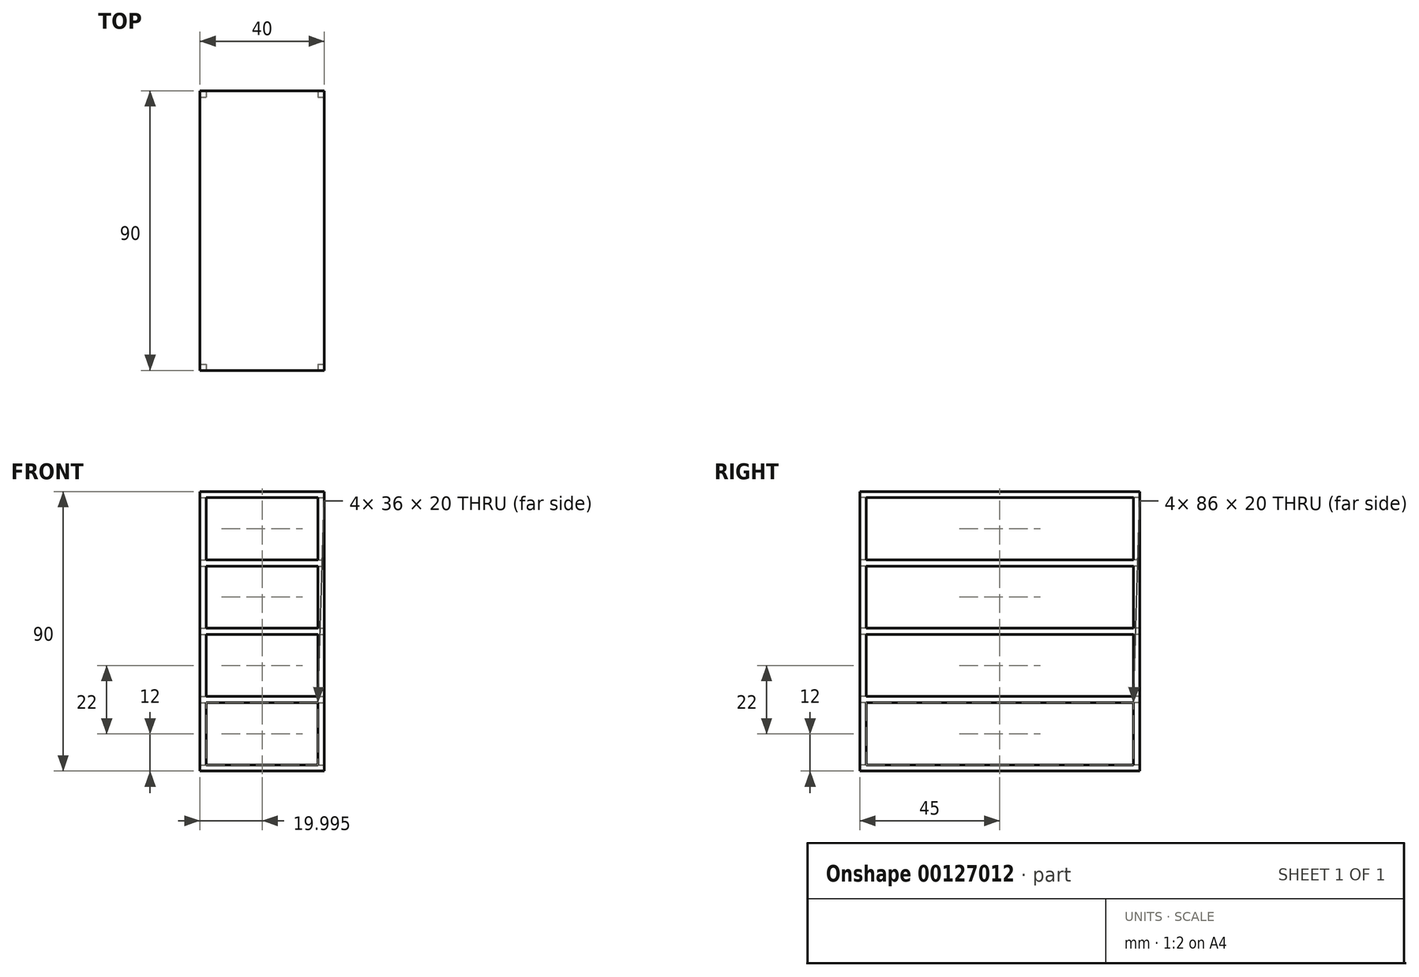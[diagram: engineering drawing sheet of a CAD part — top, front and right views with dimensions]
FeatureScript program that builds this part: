
annotation { "Feature Type Name" : "Feature", "Feature Type Description" : "" }
export const myFeature = defineFeature(function(context is Context, id is Id, definition is map)
    precondition{}
    {
        {
            var Q0;
            Q0=qCreatedBy(makeId("Top.planeOp"),FACE);
            var sketch = newSketch(context, id + "F0", { "sketchPlane" : qUnion([Q0])});
            skLineSegment(sketch, "E0.bottom", {"start": v(-46.74, 18.28) * mm, "end": v(43.26, 18.28) * mm});
            skLineSegment(sketch, "E0.top", {"start": v(-46.74, -21.72) * mm, "end": v(43.26, -21.72) * mm});
            skLineSegment(sketch, "E0.left", {"start": v(-46.74, 18.28) * mm, "end": v(-46.74, -21.72) * mm});
            skLineSegment(sketch, "E0.right", {"start": v(43.26, 18.28) * mm, "end": v(43.26, -21.72) * mm});
            skSolve(sketch);
        }
        {
            var Q0;
            Q0=makeQuery(id+"F0.imprint","IMPRINT",FACE,{"disambiguationData":[TD([[makeQuery(id+"F0.imprint","IMPRINT",EDGE,{"derivedFrom":sQuery(id+"F0.wireOp",EDGE,"E0.bottom")}),-1.0]])]});
            extrude(context, id + "F1", {"entities" : qUnion([Q0]), "depth" : 90 * mm});
        }
        {
            var Q0;
            Q0=makeQuery(id+"F1.opExtrude","SWEPT_BODY",BODY,{"disambiguationData":[OSD([sQuery(id+"F0.wireOp",EDGE,"E0.bottom"),sQuery(id+"F0.wireOp",EDGE,"E0.top"),sQuery(id+"F0.wireOp",EDGE,"E0.left"),sQuery(id+"F0.wireOp",EDGE,"E0.right")])]});
            var Q1;
            Q1=makeQuery(id+"F1.opExtrude","SWEPT_EDGE",EDGE,{"disambiguationData":[OSD([sQuery(id+"F0.wireOp",EDGE,"E0.bottom"),sQuery(id+"F0.wireOp",EDGE,"E0.right")])]});
            transform(context, id + "F2", {"entities" : qUnion([Q0]), "transformType" : TransformType.ROTATION, "transformAxis" : qUnion([Q1]), "angle" : 90 * degree, "makeCopy" : false});
        }
        {
            var Q0;
            Q0=makeQuery(id+"F1.opExtrude","SWEPT_FACE",FACE,{"disambiguationData":[OSD([sQuery(id+"F0.wireOp",EDGE,"E0.bottom")])]});
            var sketch = newSketch(context, id + "F3", { "sketchPlane" : qUnion([Q0])});
            skLineSegment(sketch, "E1.1", {"start": v(106.28, 88) * mm, "end": v(20.28, 88) * mm});
            skLineSegment(sketch, "E2.bottom", {"start": v(20.28, 68) * mm, "end": v(106.28, 68) * mm});
            skLineSegment(sketch, "E2.left", {"start": v(20.28, 88) * mm, "end": v(20.28, 68) * mm});
            skLineSegment(sketch, "E2.right", {"start": v(106.28, 88) * mm, "end": v(106.28, 68) * mm});
            skLineSegment(sketch, "E3.0.1.0", {"start": v(106.28, 66) * mm, "end": v(20.28, 66) * mm});
            skLineSegment(sketch, "E3.0.1.1", {"start": v(20.28, 66) * mm, "end": v(20.28, 46) * mm});
            skLineSegment(sketch, "E3.0.1.2", {"start": v(20.28, 46) * mm, "end": v(106.28, 46) * mm});
            skLineSegment(sketch, "E3.0.1.3", {"start": v(106.28, 66) * mm, "end": v(106.28, 46) * mm});
            skLineSegment(sketch, "E3.0.2.0", {"start": v(106.28, 44) * mm, "end": v(20.28, 44) * mm});
            skLineSegment(sketch, "E3.0.2.1", {"start": v(20.28, 44) * mm, "end": v(20.28, 24) * mm});
            skLineSegment(sketch, "E3.0.2.2", {"start": v(20.28, 24) * mm, "end": v(106.28, 24) * mm});
            skLineSegment(sketch, "E3.0.2.3", {"start": v(106.28, 44) * mm, "end": v(106.28, 24) * mm});
            skLineSegment(sketch, "E3.0.3.0", {"start": v(106.28, 22) * mm, "end": v(20.28, 22) * mm});
            skLineSegment(sketch, "E3.0.3.1", {"start": v(20.28, 22) * mm, "end": v(20.28, 2) * mm});
            skLineSegment(sketch, "E3.0.3.2", {"start": v(20.28, 2) * mm, "end": v(106.28, 2) * mm});
            skLineSegment(sketch, "E3.0.3.3", {"start": v(106.28, 22) * mm, "end": v(106.28, 2) * mm});
            skLineSegment(sketch, "E3.direction1", {"start": v(20.28, 88) * mm, "end": v(45.28, 88) * mm, "construction": true});
            skLineSegment(sketch, "E3.direction2", {"start": v(20.28, 88) * mm, "end": v(20.28, 66) * mm, "construction": true});
            skSolve(sketch);
        }
        {
            var Q0;
            {var subQ0=sQuery(id+"F3.wireOp",EDGE,"E1.1");Q0=makeQuery(id+"F3.imprint","IMPRINT",FACE,{"disambiguationData":[TD([[makeQuery(id+"F3.imprint","IMPRINT",EDGE,{"derivedFrom":subQ0}),1.0]])]});}
            var Q1;
            {var subQ0=sQuery(id+"F3.wireOp",EDGE,"DVNTmep4-zG8a-93Jq-M7zT-MYk4NrfyYevF.bottom");Q1=makeQuery(id+"F3.imprint","IMPRINT",FACE,{"disambiguationData":[TD([[makeQuery(id+"F3.imprint","IMPRINT",EDGE,{"derivedFrom":subQ0}),1.0]])]});}
            var Q2;
            {var subQ0=sQuery(id+"F3.wireOp",EDGE,"DVNTmep4-zG8a-93Jq-M7zT-MYk4NrfyYevF.top");Q2=makeQuery(id+"F3.imprint","IMPRINT",FACE,{"disambiguationData":[TD([[makeQuery(id+"F3.imprint","IMPRINT",EDGE,{"derivedFrom":subQ0}),-1.0]])]});}
            var Q3;
            {var subQ0=sQuery(id+"F3.wireOp",EDGE,"E1.3");Q3=makeQuery(id+"F3.imprint","IMPRINT",FACE,{"disambiguationData":[TD([[makeQuery(id+"F3.imprint","IMPRINT",EDGE,{"derivedFrom":subQ0}),-1.0]])]});}
            var Q4;
            {var subQ3=sQuery(id+"F3.wireOp",EDGE,"cjwGNg3R-CZs9-iRYE-jMAN-k1Y7uE1AAfra.top");Q4=makeQuery(id+"F3.imprint","IMPRINT",FACE,{"disambiguationData":[TD([[makeQuery(id+"F3.imprint","IMPRINT",EDGE,{"derivedFrom":subQ3}),-1.0]])]});}
            var Q5;
            Q5=makeQuery(id+"F3.imprint","IMPRINT",FACE,{"disambiguationData":[TD([[makeQuery(id+"F3.imprint","IMPRINT",EDGE,{"derivedFrom":sQuery(id+"F3.wireOp",EDGE,"E3.0.1.0")}),1.0]])]});
            var Q6;
            Q6=makeQuery(id+"F3.imprint","IMPRINT",FACE,{"disambiguationData":[TD([[makeQuery(id+"F3.imprint","IMPRINT",EDGE,{"derivedFrom":sQuery(id+"F3.wireOp",EDGE,"E3.0.2.0")}),1.0]])]});
            var Q7;
            Q7=makeQuery(id+"F3.imprint","IMPRINT",FACE,{"disambiguationData":[TD([[makeQuery(id+"F3.imprint","IMPRINT",EDGE,{"derivedFrom":sQuery(id+"F3.wireOp",EDGE,"E3.0.3.0")}),1.0]])]});
            var Q8;
            Q8=makeQuery(id+"F5.imprint","IMPRINT",FACE,{"disambiguationData":[TD([[makeQuery(id+"F5.imprint","IMPRINT",EDGE,{"derivedFrom":sQuery(id+"F5.wireOp",EDGE,"E4.bottom")}),-1.0]])]});
            var Q9;
            Q9=makeQuery(id+"F5.imprint","IMPRINT",FACE,{"disambiguationData":[TD([[makeQuery(id+"F5.imprint","IMPRINT",EDGE,{"derivedFrom":sQuery(id+"F5.wireOp",EDGE,"E5.0.1.0")}),-1.0]])]});
            var Q10;
            Q10=makeQuery(id+"F5.imprint","IMPRINT",FACE,{"disambiguationData":[TD([[makeQuery(id+"F5.imprint","IMPRINT",EDGE,{"derivedFrom":sQuery(id+"F5.wireOp",EDGE,"E5.0.2.0")}),-1.0]])]});
            var Q11;
            Q11=makeQuery(id+"F5.imprint","IMPRINT",FACE,{"disambiguationData":[TD([[makeQuery(id+"F5.imprint","IMPRINT",EDGE,{"derivedFrom":sQuery(id+"F5.wireOp",EDGE,"E5.0.3.0")}),-1.0]])]});
            extrude(context, id + "F4", {"entities" : qUnion([Q0, Q1, Q2, Q3, Q4, Q5, Q6, Q7, Q8, Q9, Q10, Q11]), "operationType" : NewBodyOperationType.REMOVE, "endBound" : BoundingType.THROUGH_ALL, "oppositeDirection" : true, "depth" : 25 * mm});
        }
        {
            var Q0;
            Q0=makeQuery(id+"F1.opExtrude","SWEPT_FACE",FACE,{"disambiguationData":[OSD([sQuery(id+"F0.wireOp",EDGE,"E0.right")])]});
            var sketch = newSketch(context, id + "F5", { "sketchPlane" : qUnion([Q0])});
            skLineSegment(sketch, "E4.bottom", {"start": v(5.26, 88) * mm, "end": v(41.26, 88) * mm});
            skLineSegment(sketch, "E4.top", {"start": v(5.26, 68) * mm, "end": v(41.26, 68) * mm});
            skLineSegment(sketch, "E4.left", {"start": v(5.26, 88) * mm, "end": v(5.26, 68) * mm});
            skLineSegment(sketch, "E4.right", {"start": v(41.26, 88) * mm, "end": v(41.26, 68) * mm});
            skLineSegment(sketch, "E5.0.1.0", {"start": v(5.26, 66) * mm, "end": v(41.26, 66) * mm});
            skLineSegment(sketch, "E5.0.1.1", {"start": v(5.26, 66) * mm, "end": v(5.26, 46) * mm});
            skLineSegment(sketch, "E5.0.1.2", {"start": v(5.26, 46) * mm, "end": v(41.26, 46) * mm});
            skLineSegment(sketch, "E5.0.1.3", {"start": v(41.26, 66) * mm, "end": v(41.26, 46) * mm});
            skLineSegment(sketch, "E5.0.2.0", {"start": v(5.26, 44) * mm, "end": v(41.26, 44) * mm});
            skLineSegment(sketch, "E5.0.2.1", {"start": v(5.26, 44) * mm, "end": v(5.26, 24) * mm});
            skLineSegment(sketch, "E5.0.2.2", {"start": v(5.26, 24) * mm, "end": v(41.26, 24) * mm});
            skLineSegment(sketch, "E5.0.2.3", {"start": v(41.26, 44) * mm, "end": v(41.26, 24) * mm});
            skLineSegment(sketch, "E5.0.3.0", {"start": v(5.26, 22) * mm, "end": v(41.26, 22) * mm});
            skLineSegment(sketch, "E5.0.3.1", {"start": v(5.26, 22) * mm, "end": v(5.26, 2) * mm});
            skLineSegment(sketch, "E5.0.3.2", {"start": v(5.26, 2) * mm, "end": v(41.26, 2) * mm});
            skLineSegment(sketch, "E5.0.3.3", {"start": v(41.26, 22) * mm, "end": v(41.26, 2) * mm});
            skLineSegment(sketch, "E5.direction1", {"start": v(5.26, 88) * mm, "end": v(30.26, 88) * mm, "construction": true});
            skLineSegment(sketch, "E5.direction2", {"start": v(5.26, 88) * mm, "end": v(5.26, 66) * mm, "construction": true});
            skSolve(sketch);
        }
        {
            var Q0;
            Q0=makeQuery(id+"F5.imprint","IMPRINT",FACE,{"disambiguationData":[TD([[makeQuery(id+"F5.imprint","IMPRINT",EDGE,{"derivedFrom":sQuery(id+"F5.wireOp",EDGE,"E4.bottom")}),-1.0]])]});
            var Q1;
            Q1=makeQuery(id+"F5.imprint","IMPRINT",FACE,{"disambiguationData":[TD([[makeQuery(id+"F5.imprint","IMPRINT",EDGE,{"derivedFrom":sQuery(id+"F5.wireOp",EDGE,"E5.0.1.0")}),-1.0]])]});
            var Q2;
            Q2=makeQuery(id+"F5.imprint","IMPRINT",FACE,{"disambiguationData":[TD([[makeQuery(id+"F5.imprint","IMPRINT",EDGE,{"derivedFrom":sQuery(id+"F5.wireOp",EDGE,"E5.0.2.0")}),-1.0]])]});
            var Q3;
            Q3=makeQuery(id+"F5.imprint","IMPRINT",FACE,{"disambiguationData":[TD([[makeQuery(id+"F5.imprint","IMPRINT",EDGE,{"derivedFrom":sQuery(id+"F5.wireOp",EDGE,"E5.0.3.0")}),-1.0]])]});
            extrude(context, id + "F6", {"entities" : qUnion([Q0, Q1, Q2, Q3]), "operationType" : NewBodyOperationType.REMOVE, "endBound" : BoundingType.THROUGH_ALL, "oppositeDirection" : true, "depth" : 25 * mm});
        }
    });
